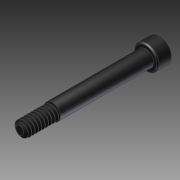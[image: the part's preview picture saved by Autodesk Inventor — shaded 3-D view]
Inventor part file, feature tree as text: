
AUTODESK INVENTOR PART (.ipt)
format: ipt  version: 2014 SP1 (Build 180222100, 222)  size: 356,864 bytes
history: native  units: in
note: dims shown in document units (in); Inventor stores cm internally (conversion verified against a paired STEP export)
features: chamfer x1, other x1, imported_body x1
ambient origin geometry x8: Origin, YZ Plane, XZ Plane, XY Plane, X Axis, Y Axis, Z Axis, Center Point
bodies: Body1 (feature_tree)
feature tree (3):
  chamfer  "Chamfer1"  [1 undecoded]
  other  "217-3423-014 Rev1.ipt1"
  imported_body  "Base1"
note: 1 required parameter value undecoded (feature->parameter linkage not recoverable at this tier; creation-order binding heuristic only, values carry confidence <= 0.55)
